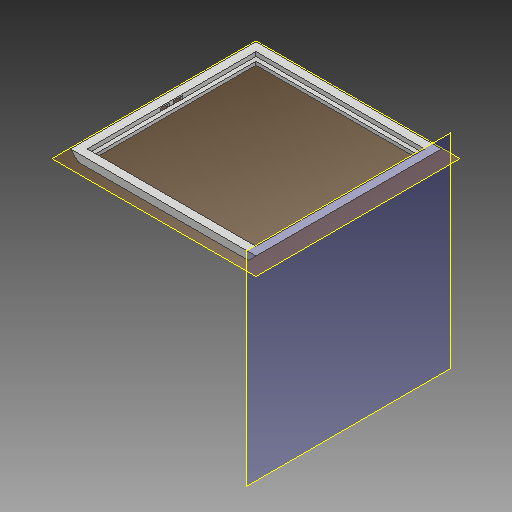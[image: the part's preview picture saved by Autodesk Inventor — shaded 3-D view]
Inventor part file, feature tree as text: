
AUTODESK INVENTOR PART (.ipt)
format: ipt  version: 2018.3 (Build 223284000, 284)  size: 206,336 bytes
history: native  units: mm
features: reference x20, other x12, extrude x6, sketch x6, plane x2, chamfer x1, projected_geometry x1
ambient origin geometry x8: Origin, YZ Plane, XZ Plane, XY Plane, X Axis, Y Axis, Z Axis, Center Point
bodies: Volumenkörper1 (feature_tree)
feature tree (48):
  extrude  "Extrusion1"  [1 undecoded]
  plane  "Arbeitsebene1"
  extrude  "Extrusion2"  Depth=10.0mm
  extrude  "Extrusion3"  Depth=10.0mm
  plane  "Arbeitsebene3"
  extrude  "Extrusion4"  Depth=8.0mm TaperAngle=0.0deg
  extrude  "Extrusion5"  Depth=2.0mm TaperAngle=0.0deg
  extrude  "Extrusion6"  Depth=18.0mm TaperAngle=45.0deg
  chamfer  "Fase2"  [1 undecoded]
  sketch  "Skizze1"  dims[d0=18.0mm d1=0.0mm d5=-20.0mm]
  reference  "Referenz1"
  reference  "Referenz2"
  reference  "Referenz3"
  reference  "Referenz4"
  reference  "Referenz5"
  sketch  "Skizze3"  dims[d6=17.0mm d7=0.0mm d8=10.0mm]
  reference  "Referenz12"
  reference  "Referenz13"
  reference  "Referenz14"
  reference  "Referenz15"
  reference  "Referenz16"
  reference  "Referenz17"
  reference  "Referenz18"
  reference  "Referenz19"
  sketch  "Skizze5"  dims[d9=10.0mm d10=10.0mm]
  sketch  "Skizze6"  dims[d11=10.0mm d12=8.0mm d13=0.0mm]
  reference  "Referenz20"
  reference  "Referenz21"
  reference  "Referenz22"
  reference  "Referenz23"
  reference  "Referenz24"
  reference  "Referenz25"
  sketch  "Skizze7"  dims[d14=25.0mm d15=0.0mm d16=2.0mm d17=0.0mm]
  projected_geometry  "Projizierte Kontur1"
  sketch  "Skizze8"  dims[d18=2.0mm d19=0.0mm d20=18.0mm d21=2.0mm d22=45.0deg]
  reference  "Referenz26"
  parser-record x2  (decoder bookkeeping rows leaked as tree rows — omitted from the tree; the rows remain in map.json)
  other  "SmartCube_Quadratisch.iam"
  other  "Wand2_MIR:1"
  other  "Wand1:1"
  other  "Wand1_MIR:1"
  other  "Wand2:1"
  other  "PV_Modul:1"
  other  "<userpath>\Documents\Dipl\Smartcube_Construction\Version_3\Baugruppe1.iam"
  other  "Baugruppe1.iam"
  other  "PV_Ramen_CPY_3_2:1"
  other  "PV_Modul_CPY_3_CPY:1"
note: 2 required parameter values undecoded (feature->parameter linkage not recoverable at this tier; creation-order binding heuristic only, values carry confidence <= 0.55)
note: 2 file-system paths scrubbed to <path> (originals preserved in map.json)
